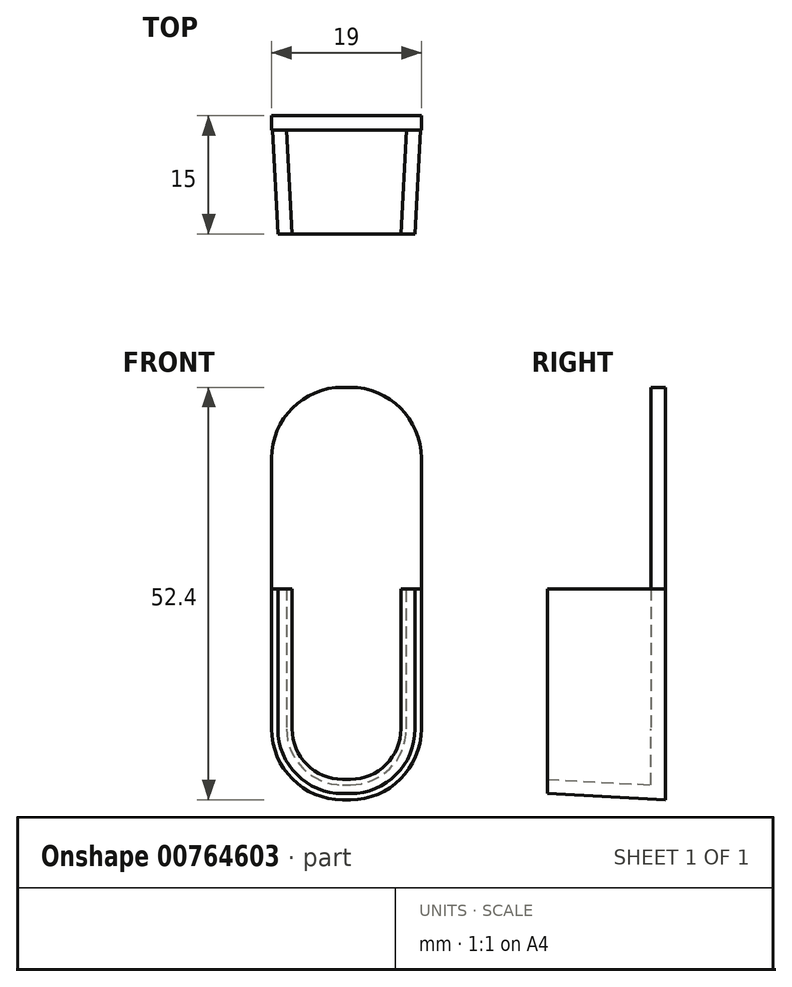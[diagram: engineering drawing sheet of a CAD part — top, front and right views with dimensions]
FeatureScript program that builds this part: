
annotation { "Feature Type Name" : "Feature", "Feature Type Description" : "" }
export const myFeature = defineFeature(function(context is Context, id is Id, definition is map)
    precondition{}
    {
        {
            var Q0;
            Q0=qCreatedBy(makeId("Front.planeOp"),FACE);
            var sketch = newSketch(context, id + "F0", { "sketchPlane" : qUnion([Q0])});
            skPoint(sketch, "E0.middle", {"position": v(0, 0) * mm});
            skPoint(sketch, "E1.visualSharp", {"position": v(7.5, 17.5) * mm});
            skPoint(sketch, "E2.visualSharp", {"position": v(-7.5, 17.5) * mm});
            skPoint(sketch, "E3.visualSharp", {"position": v(-7.5, -17.5) * mm});
            skPoint(sketch, "E4.visualSharp", {"position": v(7.5, -17.5) * mm});
            skArc(sketch, "E5.0", {"start": v(-0.5, 19.5) * mm, "mid": v(-6.86, 16.86) * mm, "end": v(-9.5, 10.5) * mm});
            skLineSegment(sketch, "E5.1", {"start": v(0.5, 19.5) * mm, "end": v(-0.5, 19.5) * mm});
            skLineSegment(sketch, "E5.2", {"start": v(-9.5, 10.5) * mm, "end": v(-9.5, -10.5) * mm});
            skArc(sketch, "E5.3", {"start": v(9.5, 10.5) * mm, "mid": v(6.86, 16.86) * mm, "end": v(0.5, 19.5) * mm});
            skArc(sketch, "E5.4", {"start": v(-9.5, -10.5) * mm, "mid": v(-6.86, -16.86) * mm, "end": v(-0.5, -19.5) * mm});
            skLineSegment(sketch, "E5.5", {"start": v(0.5, -19.5) * mm, "end": v(-0.5, -19.5) * mm});
            skArc(sketch, "E5.6", {"start": v(0.5, -19.5) * mm, "mid": v(6.86, -16.86) * mm, "end": v(9.5, -10.5) * mm});
            skLineSegment(sketch, "E5.7", {"start": v(9.5, 10.5) * mm, "end": v(9.5, -10.5) * mm});
            skSolve(sketch);
        }
        {
            var Q0;
            Q0=makeQuery(id+"F0.imprint","IMPRINT",FACE,{"disambiguationData":[TD([[makeQuery(id+"F0.imprint","IMPRINT",EDGE,{"derivedFrom":sQuery(id+"F0.wireOp",EDGE,"E5.0")}),1.0]])]});
            extrude(context, id + "F1", {"entities" : qUnion([Q0]), "depth" : 15 * mm, "offsetDistance" : 25 * mm, "hasDraft" : true, "draftAngle" : 0.05 * radian, "draftPullDirection" : true});
        }
        {
            var Q0;
            Q0=makeQuery(id+"F1.opExtrude","CAP_FACE",FACE,{"disambiguationData":[OSD([sQuery(id+"F0.wireOp",EDGE,"E5.0"),sQuery(id+"F0.wireOp",EDGE,"E5.1"),sQuery(id+"F0.wireOp",EDGE,"E5.2"),sQuery(id+"F0.wireOp",EDGE,"E5.3"),sQuery(id+"F0.wireOp",EDGE,"E5.4"),sQuery(id+"F0.wireOp",EDGE,"E5.5"),sQuery(id+"F0.wireOp",EDGE,"E5.6"),sQuery(id+"F0.wireOp",EDGE,"E5.7")])],"isStart":true});
            var Q1;
            Q1=makeQuery(id+"F1.opExtrude","CAP_FACE",FACE,{"disambiguationData":[OSD([sQuery(id+"F0.wireOp",EDGE,"E5.0"),sQuery(id+"F0.wireOp",EDGE,"E5.1"),sQuery(id+"F0.wireOp",EDGE,"E5.2"),sQuery(id+"F0.wireOp",EDGE,"E5.3"),sQuery(id+"F0.wireOp",EDGE,"E5.4"),sQuery(id+"F0.wireOp",EDGE,"E5.5"),sQuery(id+"F0.wireOp",EDGE,"E5.6"),sQuery(id+"F0.wireOp",EDGE,"E5.7")])],"isStart":false});
            shell(context, id + "F2", {"entities" : qUnion([Q0, Q1]), "thickness" : 1.8 * mm});
        }
        {
            var Q0;
            Q0=qCreatedBy(makeId("Right.planeOp"),FACE);
            var sketch = newSketch(context, id + "F3", { "sketchPlane" : qUnion([Q0])});
            skLineSegment(sketch, "E6.bottom", {"start": v(0, 24.34) * mm, "end": v(-16.79, 24.34) * mm});
            skLineSegment(sketch, "E6.top", {"start": v(0, 7.3) * mm, "end": v(-16.79, 7.3) * mm});
            skLineSegment(sketch, "E6.left", {"start": v(0, 24.34) * mm, "end": v(0, 7.3) * mm});
            skLineSegment(sketch, "E6.right", {"start": v(-16.79, 24.34) * mm, "end": v(-16.79, 7.3) * mm});
            skSolve(sketch);
        }
        {
            var Q0;
            Q0=makeQuery(id+"F3.imprint","IMPRINT",FACE,{"disambiguationData":[TD([[makeQuery(id+"F3.imprint","IMPRINT",EDGE,{"derivedFrom":sQuery(id+"F3.wireOp",EDGE,"E6.bottom")}),1.0]])]});
            extrude(context, id + "F4", {"entities" : qUnion([Q0]), "operationType" : NewBodyOperationType.REMOVE, "endBound" : BoundingType.SYMMETRIC, "oppositeDirection" : true, "depth" : 56 * mm, "offsetDistance" : 25 * mm});
        }
        {
            var Q0;
            Q0=makeQuery(id+"F1.opExtrude","CAP_FACE",FACE,{"disambiguationData":[OSD([sQuery(id+"F0.wireOp",EDGE,"E5.0"),sQuery(id+"F0.wireOp",EDGE,"E5.1"),sQuery(id+"F0.wireOp",EDGE,"E5.2"),sQuery(id+"F0.wireOp",EDGE,"E5.3"),sQuery(id+"F0.wireOp",EDGE,"E5.4"),sQuery(id+"F0.wireOp",EDGE,"E5.5"),sQuery(id+"F0.wireOp",EDGE,"E5.6"),sQuery(id+"F0.wireOp",EDGE,"E5.7")])],"isStart":true});
            var sketch = newSketch(context, id + "F5", { "sketchPlane" : qUnion([Q0])});
            skPoint(sketch, "E7.middle", {"position": v(0, 0) * mm});
            skPoint(sketch, "E8.visualSharp", {"position": v(7.5, 30.9) * mm});
            skPoint(sketch, "E9.visualSharp", {"position": v(-7.5, 30.9) * mm});
            skPoint(sketch, "E10.visualSharp", {"position": v(-7.5, -17.5) * mm});
            skPoint(sketch, "E11.visualSharp", {"position": v(7.5, -17.5) * mm});
            skArc(sketch, "E12.0", {"start": v(-0.5, 32.9) * mm, "mid": v(-6.86, 30.26) * mm, "end": v(-9.5, 23.9) * mm});
            skLineSegment(sketch, "E12.1", {"start": v(0.5, 32.9) * mm, "end": v(-0.5, 32.9) * mm});
            skLineSegment(sketch, "E12.2", {"start": v(-9.5, 23.9) * mm, "end": v(-9.5, -10.5) * mm});
            skArc(sketch, "E12.3", {"start": v(9.5, 23.9) * mm, "mid": v(6.86, 30.26) * mm, "end": v(0.5, 32.9) * mm});
            skArc(sketch, "E12.4", {"start": v(-9.5, -10.5) * mm, "mid": v(-6.86, -16.86) * mm, "end": v(-0.5, -19.5) * mm});
            skLineSegment(sketch, "E12.5", {"start": v(0.5, -19.5) * mm, "end": v(-0.5, -19.5) * mm});
            skArc(sketch, "E12.6", {"start": v(0.5, -19.5) * mm, "mid": v(6.86, -16.86) * mm, "end": v(9.5, -10.5) * mm});
            skLineSegment(sketch, "E12.7", {"start": v(9.5, 23.9) * mm, "end": v(9.5, -10.5) * mm});
            skSolve(sketch);
        }
        {
            var Q0;
            {var subQ12=sQuery(id+"F5.wireOp",EDGE,"E12.0");Q0=makeQuery(id+"F5.imprint","IMPRINT",FACE,{"disambiguationData":[TD([[makeQuery(id+"F5.imprint","IMPRINT",EDGE,{"derivedFrom":subQ12}),1.0]])]});}
            extrude(context, id + "F6", {"entities" : qUnion([Q0]), "operationType" : NewBodyOperationType.ADD, "oppositeDirection" : true, "depth" : 1.8 * mm, "offsetDistance" : 25 * mm});
        }
    });
